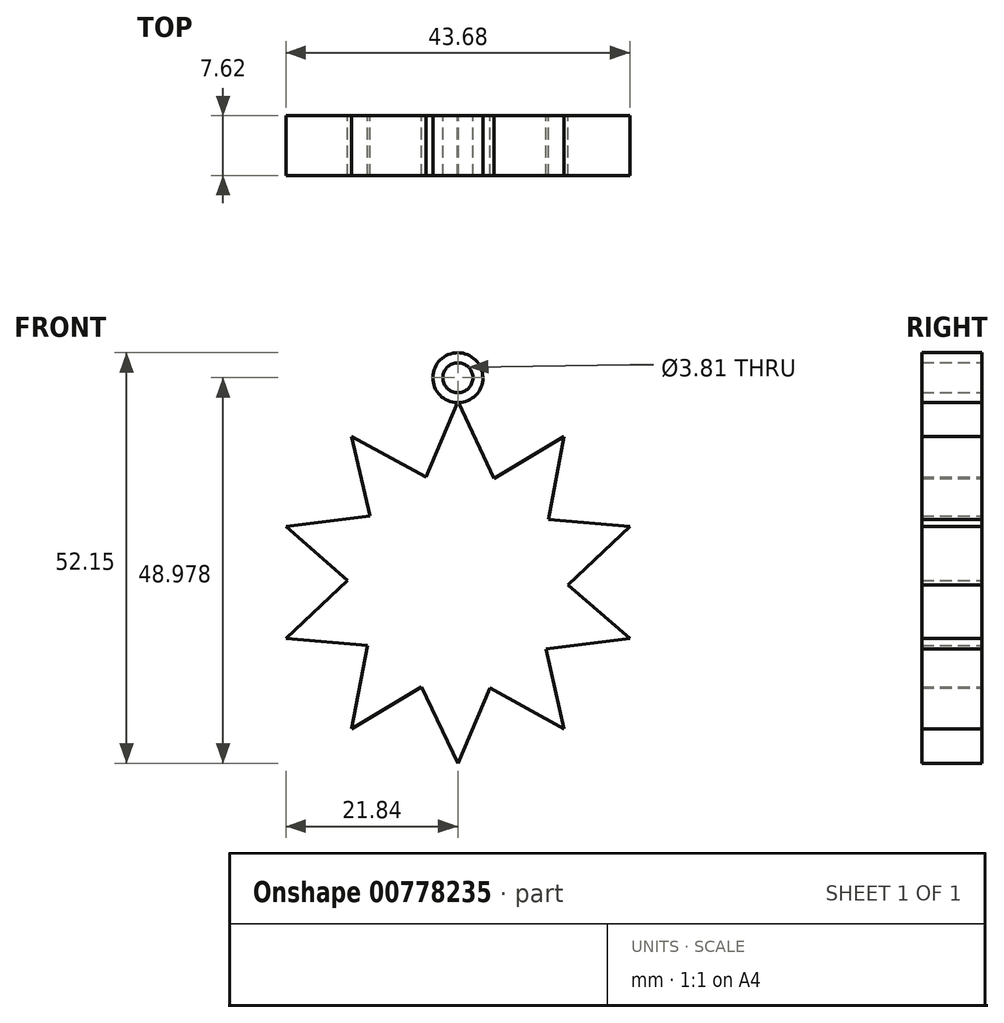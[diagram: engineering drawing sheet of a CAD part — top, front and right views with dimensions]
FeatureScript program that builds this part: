
annotation { "Feature Type Name" : "Feature", "Feature Type Description" : "" }
export const myFeature = defineFeature(function(context is Context, id is Id, definition is map)
    precondition{}
    {
        {
            var Q0;
            Q0=qCreatedBy(makeId("Front.planeOp"),FACE);
            var sketch = newSketch(context, id + "F0", { "sketchPlane" : qUnion([Q0])});
            skCircle(sketch, "E0", {"center": v(0, 0) * mm, "radius": 12.7 * mm});
            skLineSegment(sketch, "E1", {"start": v(0, 22.96) * mm, "end": v(5.43, 11.48) * mm});
            skLineSegment(sketch, "E2", {"start": v(0, 22.96) * mm, "end": v(-4.77, 11.77) * mm});
            skLineSegment(sketch, "E3.1.0", {"start": v(-13.5, 18.58) * mm, "end": v(-10.78, 6.72) * mm});
            skLineSegment(sketch, "E3.1.1", {"start": v(-13.5, 18.58) * mm, "end": v(-2.36, 12.48) * mm});
            skLineSegment(sketch, "E3.2.0", {"start": v(-21.84, 7.1) * mm, "end": v(-12.67, -0.9) * mm});
            skLineSegment(sketch, "E3.2.1", {"start": v(-21.84, 7.1) * mm, "end": v(-9.24, 8.7) * mm});
            skLineSegment(sketch, "E3.3.0", {"start": v(-21.84, -7.1) * mm, "end": v(-9.72, -8.17) * mm});
            skLineSegment(sketch, "E3.3.1", {"start": v(-21.84, -7.1) * mm, "end": v(-12.6, 1.61) * mm});
            skLineSegment(sketch, "E3.4.0", {"start": v(-13.5, -18.58) * mm, "end": v(-3.06, -12.33) * mm});
            skLineSegment(sketch, "E3.4.1", {"start": v(-13.5, -18.58) * mm, "end": v(-11.14, -6.1) * mm});
            skLineSegment(sketch, "E3.5.0", {"start": v(0, -22.96) * mm, "end": v(4.77, -11.77) * mm});
            skLineSegment(sketch, "E3.5.1", {"start": v(0, -22.96) * mm, "end": v(-5.43, -11.48) * mm});
            skLineSegment(sketch, "E3.6.0", {"start": v(13.5, -18.58) * mm, "end": v(10.78, -6.72) * mm});
            skLineSegment(sketch, "E3.6.1", {"start": v(13.5, -18.58) * mm, "end": v(2.36, -12.48) * mm});
            skLineSegment(sketch, "E3.7.0", {"start": v(21.84, -7.1) * mm, "end": v(12.67, 0.9) * mm});
            skLineSegment(sketch, "E3.7.1", {"start": v(21.84, -7.1) * mm, "end": v(9.24, -8.7) * mm});
            skLineSegment(sketch, "E3.8.0", {"start": v(21.84, 7.1) * mm, "end": v(9.72, 8.17) * mm});
            skLineSegment(sketch, "E3.8.1", {"start": v(21.84, 7.1) * mm, "end": v(12.6, -1.61) * mm});
            skLineSegment(sketch, "E3.9.0", {"start": v(13.5, 18.58) * mm, "end": v(3.06, 12.33) * mm});
            skLineSegment(sketch, "E3.9.1", {"start": v(13.5, 18.58) * mm, "end": v(11.14, 6.1) * mm});
            skCircle(sketch, "E4", {"center": v(0, 26.02) * mm, "radius": 3.18 * mm});
            skCircle(sketch, "E5", {"center": v(0, 26.02) * mm, "radius": 1.9 * mm});
            skSolve(sketch);
        }
        {
            var Q0;
            Q0 = qSketchRegion(id + "F0", true);
            var Q1;
            {var subQ0=sQuery(id+"F0.wireOp",EDGE,"E0");var subQ8=makeQuery(id+"F0.imprint","INTERSECT",VERTEX,{"derivedFrom":[subQ0,sQuery(id+"F0.wireOp",EDGE,"E3.7.0")]});Q1=makeQuery(id+"F0.imprint","IMPRINT",FACE,{"disambiguationData":[TD([[makeQuery(id+"F0.imprint","IMPRINT",EDGE,{"disambiguationData":[TD([[subQ8,-1.0]])],"derivedFrom":subQ0}),1.0]])]});}
            extrude(context, id + "F1", {"entities" : qUnion([Q0, Q1]), "depth" : 7.62 * mm, "offsetDistance" : 25.4 * mm});
        }
    });
